# Revit family: NAU_Naughtone_OffcStrg_Sideboard
name_source: partatom
category: Furniture
revit_build: Autodesk Revit 2015 (Build: 20140903_1530(x64)
units: mm (PartAtom-declared; Revit-internal decimal feet)

## types (3) — shared parameters
Additional Materials = Additional material and finish options available. Please contact Naughtone direct for further information.
Assembly Code = E2020200
AssetType = Movable
BIMObjectName = NAU_Naughtone_OfficeStorage_Sideboard
Category = Pr_40_30_78_81 : Sideboards
DurationUnit = year
IfcExportAs = IfcFurnishingElementType
IfcExportType = SIDEBOARD
Keynote = Pr_40_30_78_81
ManufacturerAddress = Knaresborough Tech Park, Manse Lane, Knaresborough, HG5 8LF
ManufacturerName = Naughtone
ManufacturerURL = www.naughtone.com
NBSDescription = Office storage
NBSReference = 45-35-80/360
Name = OfficeStorage_Sideboard_Naughtone
NominalHeight = 750 mm  [stored 2.46063 ft]
NominalWidth = 500 mm  [stored 1.64042 ft]
ProductInformation = www.naughtone.com/products/sideboard/
Revision = 1
Shape = Rectangular
Type Comments = Sideboard
URL = www.naughtone.com
Uniclass2015Code = Pr_40_30_78_81
Uniclass2015Title = Sideboards
Uniclass2015Version = Products v1.10
Version = 1
WarrantyDescription = Request warranty information from naughtone
WarrantyDurationLabor = 5
WarrantyDurationParts = 5
WarrantyDurationUnit = year
zero-valued in all types: Cost, NumberOfChairs

## per-type parameters (varying)
| type | Description | Door 1200mm | Door 1600mm | Door 2000mm | Hinge Frame 1600mm | Hinge Frame 2000mm | ModelReference | NominalLength | Size | Sled Leg | Sled Leg 1200mm | WorksurfaceArea |
| SB20 | Sideboard 2000 | No | No | Yes | No | Yes | Sideboard 2000 | 2000 mm  [stored 6.56168 ft] | 2000 x 500 x 750mm | Yes | No | 1 m² |
| SB16 | Sideboard 1600 | No | Yes | No | Yes | No | Sideboard 1600 | 1600 mm  [stored 5.24934 ft] | 1600 x 500 x 750mm | Yes | No | 0.8 m² |
| SB12 | Sideboard 1200 | Yes | No | No | No | No | Sideboard 1200 | 1200 mm | 1200 x 500 x 750mm | No | Yes | 0.6 m² |

note: column(s) folded — value = type name in every type: Model, ModelNumber

note: [stored X ft] marks values corroborated as IEEE doubles in the binary element streams (Revit-internal decimal feet)

## geometry (parser evidence)
native form markers: Sweep x27
no freeform markers — native parametric forms only
